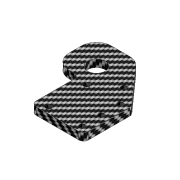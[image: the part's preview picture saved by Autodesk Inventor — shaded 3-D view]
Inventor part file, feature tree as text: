
AUTODESK INVENTOR PART (.ipt)
format: ipt  version: 2022 (Build 260153000, 153)  size: 168,448 bytes
history: native  units: mm
features: fillet x2, sketch x2, extrude x1, projected_geometry x1
ambient origin geometry x8: Origin, YZ Plane, XZ Plane, XY Plane, X Axis, Y Axis, Z Axis, Center Point
bodies: Solid1 (feature_tree)
feature tree (6):
  extrude  "Extrusion1"  Depth=21.0mm
  fillet  "Fillet1"  Radius=1.0mm
  fillet  "Fillet2"  Radius=7.0mm
  sketch  "Sketch2"  dims[d4=16.0mm d5=10.0mm d6=10.0mm d8=6.0mm d9=2.3mm d10=1.5mm d11=2.3mm d12=3.0mm d13=4.5mm d14=1.5mm d15=2.3mm d16=1.5mm d17=3.0mm d18=2.3mm d19=4.5mm d20=1.5mm d21=3.0mm d22=0.0mm d23=2.0mm d24=6.0mm d25=2.3mm d26=14.1mm d27=8.0mm d28=2.3mm d29=3.0mm]
  sketch  "Sketch1"  dims[d0=9.1mm d1=21.0mm d2=1.0mm d3=7.0mm]
  projected_geometry  "Projected Loop1"
